# Revit family: Connectorail WF family
name_source: partatom
category: Generic Models
units: mm (PartAtom-declared; Revit-internal decimal feet)

## family parameters
Always vertical = Yes
Can host rebar = No
Cut with Voids When Loaded = No
Host = Wall
Maintain Annotation Orientation = No
Part Type = Normal
Room Calculation Point = No
Round Connector Dimension = Use Diameter
Shared = No

## types (1)
- Connectorail WF family
    Default Elevation = 0' - 0"
    Description = Julius Blum and Co.,Inc. 
Connectorail® Water Fountain Railing system,
Includes the following part numbers - 
Cover Flange /Floor Flange : 710
90 Miter Elbow: 7411
90 Tee Connection: 7440
High Strength Connectorail® Post 50": 7404

System available in other pipe size and metals
System also available in clear anodized, notated by "-A" 

For Pipe Size 1 1/4 sch. 40
    Manufacturer = Julius Blum and Co.,Inc.
    Model = Connectorail® Water Fountain Railing System
    URL = https://www.juliusblum.com

## geometry (parser evidence)
native form markers: Sweep x2
no freeform markers — native parametric forms only
